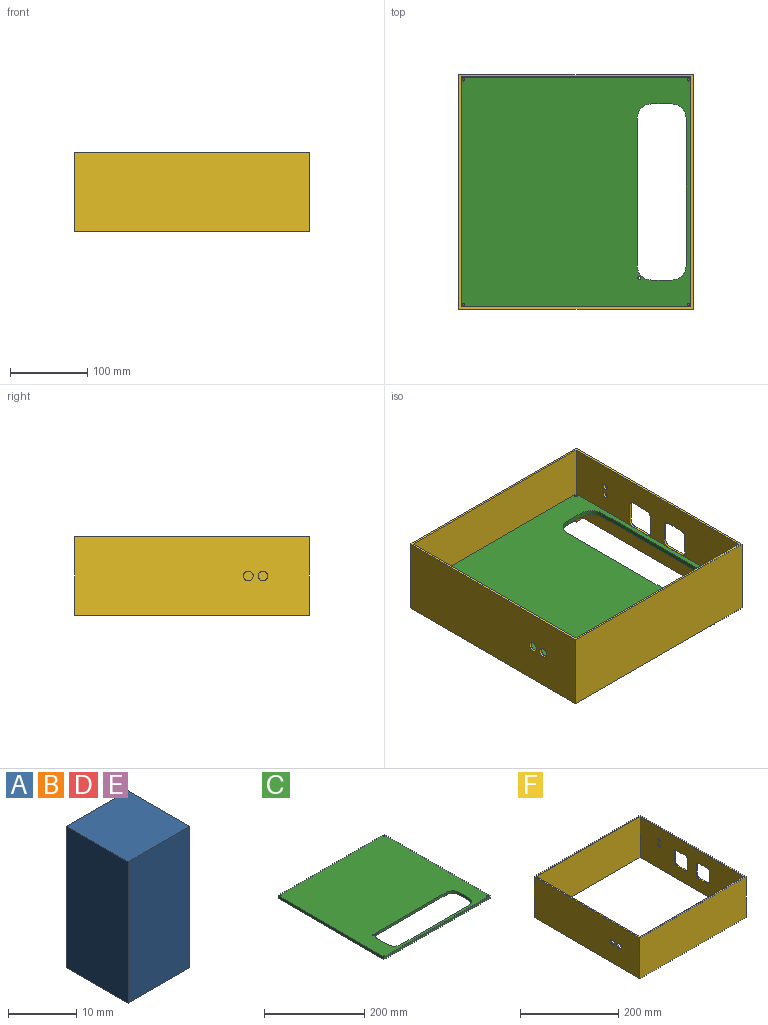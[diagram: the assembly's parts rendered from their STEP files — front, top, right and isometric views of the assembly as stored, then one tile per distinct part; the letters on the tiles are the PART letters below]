
ASSEMBLY  parts=6 mates=5
PART A: 6 faces, bbox 12.7x12.7x25.4 mm
  f0: plane 25.4x12.7mm, normal (0,-1,0), area 322.6mm2, adj f1,f3,f4,f5
  f1: plane 25.4x12.7mm, normal (1,0,0), area 322.6mm2, adj f0,f2,f4,f5
  f2: plane 25.4x12.7mm, normal (0,1,0), area 322.6mm2, adj f1,f3,f4,f5
  f3: plane 25.4x12.7mm, normal (-1,0,0), area 322.6mm2, adj f0,f2,f4,f5
  f4: plane 12.7x12.7mm, normal (0,0,1), area 161.3mm2, adj f0,f1,f2,f3
  f5: plane 12.7x12.7mm, normal (0,0,-1), area 161.3mm2, adj f0,f1,f2,f3
PART B: same geometry as A
PART C: 19 faces, bbox 298.5x298.5x6.4 mm
  f0: plane 25.4x6.35mm, normal (1,0,0), area 161.3mm2, adj f1,f10,f17,f18
  f1: cylinder r=19.05mm len=19.05mm, axis (0,0,-1), area 190mm2, adj f0,f2,f17,f18
  f2: plane 190.5x6.35mm, normal (0,-1,0), area 1209.7mm2, adj f1,f3,f17,f18
  f3: cylinder r=19.05mm len=19.05mm, axis (0,0,-1), area 190mm2, adj f2,f4,f17,f18
  f4: plane 25.4x6.35mm, normal (-1,0,0), area 161.3mm2, adj f3,f5,f17,f18
  f5: cylinder r=19.05mm len=19.05mm, axis (0,0,-1), area 190mm2, adj f4,f6,f17,f18
  f6: plane 190.5x6.35mm, normal (0,1,0), area 1209.7mm2, adj f5,f10,f17,f18
  f7: plane 298.45x6.35mm, normal (0,-1,0), area 1895.2mm2, adj f8,f14,f17,f18
  f8: plane 298.45x6.35mm, normal (1,0,0), area 1895.2mm2, adj f7,f9,f17,f18
  f9: plane 298.45x6.35mm, normal (0,1,0), area 1895.2mm2, adj f8,f14,f17,f18
  f10: cylinder r=19.05mm len=19.05mm, axis (0,0,-1), area 190mm2, adj f0,f6,f17,f18
  f11: cylinder r=1.91mm len=6.35mm, axis (0,0,-1), area 76mm2, adj f17,f18
  f12: cylinder r=1.91mm len=6.35mm, axis (0,0,-1), area 76mm2, adj f17,f18
  f13: cylinder r=1.91mm len=6.35mm, axis (0,0,-1), area 76mm2, adj f17,f18
  f14: plane 298.45x6.35mm, normal (-1,0,0), area 1895.2mm2, adj f7,f9,f17,f18
  f15: cylinder r=1.91mm len=6.35mm, axis (0,0,-1), area 76mm2, adj f17,f18
  f16: cylinder r=1.91mm len=6.35mm, axis (0,0,-1), area 76mm2, adj f17,f18
  f17: plane 298.45x298.45mm, normal (0,0,1), area 74810.8mm2, adj f0,f1,f2,f3,f4,f5,f6,f7
  f18: plane 298.45x298.45mm, normal (0,0,-1), area 74810.8mm2, adj f0,f1,f2,f3,f4,f5,f6,f7
PART D: same geometry as A
PART E: same geometry as A
PART F: 30 faces, bbox 304.8x304.8x101.6 mm
  f0: plane 304.8x101.6mm, normal (1,0,0), area 28042.5mm2, adj f2,f3,f4,f6,f10,f11,f12,f13
  f1: plane 298.45x101.6mm, normal (-1,0,0), area 27397.3mm2, adj f2,f3,f8,f9,f10,f11,f12,f13
  f2: plane 304.8x304.8mm, normal (0,0,1), area 3830.6mm2, adj f0,f1,f4,f5,f6,f7,f8,f9
  f3: plane 304.8x304.8mm, normal (0,0,-1), area 3830.6mm2, adj f0,f1,f4,f5,f6,f7,f8,f9
  f4: plane 304.8x101.6mm, normal (0,1,0), area 30967.7mm2, adj f0,f2,f3,f5
  f5: plane 304.8x101.6mm, normal (-1,0,0), area 30714.3mm2, adj f2,f3,f4,f6,f26,f27
  f6: plane 304.8x101.6mm, normal (0,-1,0), area 30967.7mm2, adj f0,f2,f3,f5
  f7: plane 298.45x101.6mm, normal (1,0,0), area 30069.2mm2, adj f2,f3,f8,f9,f26,f27
  f8: plane 298.45x101.6mm, normal (0,1,0), area 30322.5mm2, adj f1,f2,f3,f7
  f9: plane 298.45x101.6mm, normal (0,-1,0), area 30322.5mm2, adj f1,f2,f3,f7
  f10: cylinder r=6.35mm len=6.35mm, axis (1,0,0), area 31.7mm2, adj f0,f1,f11,f17
  f11: plane 25.4x3.18mm, normal (0,1,0), area 80.6mm2, adj f0,f1,f10,f12
  f12: cylinder r=6.35mm len=6.35mm, axis (1,0,0), area 31.7mm2, adj f0,f1,f11,f13
  f13: plane 25.4x3.18mm, normal (0,0,1), area 80.6mm2, adj f0,f1,f12,f14
  f14: cylinder r=6.35mm len=6.35mm, axis (1,0,0), area 31.7mm2, adj f0,f1,f13,f15
  f15: plane 25.4x3.18mm, normal (0,-1,0), area 80.6mm2, adj f0,f1,f14,f16
  f16: cylinder r=6.35mm len=6.35mm, axis (1,0,0), area 31.7mm2, adj f0,f1,f15,f17
  f17: plane 25.4x3.18mm, normal (0,0,-1), area 80.6mm2, adj f0,f1,f10,f16
  f18: plane 25.4x3.18mm, normal (0,-1,0), area 80.6mm2, adj f0,f1,f19,f25
  f19: cylinder r=6.35mm len=6.35mm, axis (1,0,0), area 31.7mm2, adj f0,f1,f18,f20
  f20: plane 25.4x3.18mm, normal (0,0,-1), area 80.6mm2, adj f0,f1,f19,f21
  f21: cylinder r=6.35mm len=6.35mm, axis (1,0,0), area 31.7mm2, adj f0,f1,f20,f22
  f22: plane 25.4x3.18mm, normal (0,1,0), area 80.6mm2, adj f0,f1,f21,f23
  f23: cylinder r=6.35mm len=6.35mm, axis (1,0,0), area 31.7mm2, adj f0,f1,f22,f24
  f24: plane 25.4x3.18mm, normal (0,0,1), area 80.6mm2, adj f0,f1,f23,f25
  f25: cylinder r=6.35mm len=6.35mm, axis (1,0,0), area 31.7mm2, adj f0,f1,f18,f24
  f26: cylinder r=6.35mm len=12.7mm, axis (-1,0,0), area 126.7mm2, adj f5,f7
  f27: cylinder r=6.35mm len=12.7mm, axis (-1,0,0), area 126.7mm2, adj f5,f7
  f28: cylinder r=3.81mm len=7.62mm, axis (1,0,0), area 76mm2, adj f0,f1
  f29: cylinder r=3.81mm len=7.62mm, axis (1,0,0), area 76mm2, adj f0,f1
PLACE A t=(-131.98,125.69,-86.01)mm
PLACE B t=(153.77,125.69,-86.01)mm
PLACE C rot(axis=(0,0,1),90deg) t=(10.89,-17.19,-60.61)mm
PLACE D t=(-131.98,-160.06,-86.01)mm
PLACE E t=(153.77,-160.06,-86.01)mm
PLACE F t=(-141.51,135.21,-86.01)mm
MATE fastened C.f18 <-> B.f4  axis (0,0,-1) through (160.12,132.04,-60.61)mm
MATE fastened B.f1 <-> F.f1  axis (1,0,0) through (160.12,132.04,-86.01)mm
MATE fastened D.f3 <-> F.f7  axis (-1,0,0) through (-138.33,-166.41,-86.01)mm
MATE fastened A.f2 <-> F.f9  axis (0,1,0) through (-138.33,132.04,-86.01)mm
MATE fastened E.f0 <-> F.f8  axis (0,-1,0) through (160.12,-166.41,-86.01)mm
